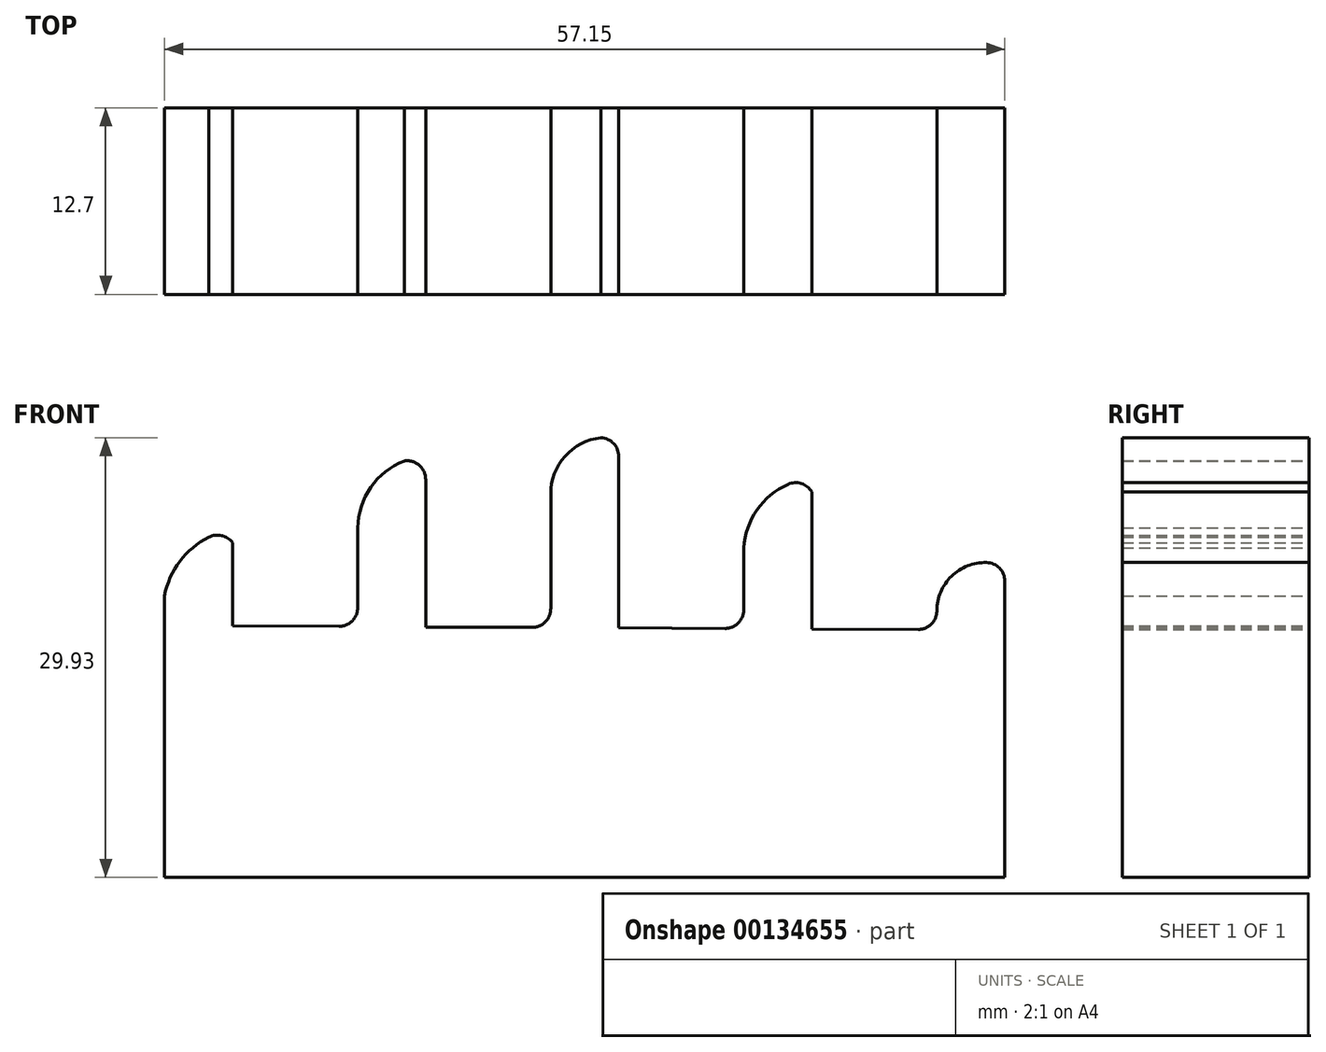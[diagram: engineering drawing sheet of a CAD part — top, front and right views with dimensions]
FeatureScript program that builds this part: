
annotation { "Feature Type Name" : "Feature", "Feature Type Description" : "" }
export const myFeature = defineFeature(function(context is Context, id is Id, definition is map)
    precondition{}
    {
        {
            var Q0;
            Q0=qCreatedBy(makeId("Front.planeOp"),FACE);
            var sketch = newSketch(context, id + "F0", { "sketchPlane" : qUnion([Q0])});
            skLineSegment(sketch, "E0", {"start": v(-7.96, 21.1) * mm, "end": v(-7.96, 21.1) * mm});
            skLineSegment(sketch, "E1", {"start": v(-8.39, 0) * mm, "end": v(-65.54, 0) * mm});
            skArc(sketch, "E2.filletArc", {"start": v(-23.14, 26.76) * mm, "mid": v(-25.25, 25) * mm, "end": v(-26.14, 22.42) * mm});
            skArc(sketch, "E3.filletArc", {"start": v(-60.92, 22.78) * mm, "mid": v(-61.66, 23.27) * mm, "end": v(-62.53, 23.15) * mm});
            skArc(sketch, "E4.filletArc", {"start": v(-47.78, 27.1) * mm, "mid": v(-48.23, 28.05) * mm, "end": v(-49.24, 28.35) * mm});
            skArc(sketch, "E5.filletArc", {"start": v(-34.65, 28.66) * mm, "mid": v(-35, 29.53) * mm, "end": v(-35.86, 29.93) * mm});
            skArc(sketch, "E6.filletArc", {"start": v(-21.52, 26.23) * mm, "mid": v(-22.23, 26.8) * mm, "end": v(-23.14, 26.76) * mm});
            skArc(sketch, "E7.filletArc", {"start": v(-8.39, 20.16) * mm, "mid": v(-8.75, 21.05) * mm, "end": v(-9.63, 21.43) * mm});
            skPoint(sketch, "E8.endSnap0", {"position": v(-36.53, 17) * mm});
            skLineSegment(sketch, "E9", {"start": v(-60.92, 22.78) * mm, "end": v(-60.92, 17.12) * mm});
            skLineSegment(sketch, "E10", {"start": v(-47.78, 27.1) * mm, "end": v(-47.78, 17.05) * mm});
            skLineSegment(sketch, "E11", {"start": v(-34.65, 28.66) * mm, "end": v(-34.65, 16.99) * mm});
            skLineSegment(sketch, "E12", {"start": v(-26.14, 22.42) * mm, "end": v(-26.14, 18.22) * mm});
            skLineSegment(sketch, "E13", {"start": v(-21.52, 26.23) * mm, "end": v(-21.52, 16.9) * mm});
            skLineSegment(sketch, "E14", {"start": v(-60.92, 17.12) * mm, "end": v(-53.68, 17.09) * mm});
            skLineSegment(sketch, "E15", {"start": v(-47.78, 17.05) * mm, "end": v(-40.55, 17.02) * mm});
            skLineSegment(sketch, "E16", {"start": v(-34.65, 16.99) * mm, "end": v(-27.42, 16.95) * mm});
            skLineSegment(sketch, "E17", {"start": v(-21.52, 16.9) * mm, "end": v(-14.29, 16.88) * mm});
            skArc(sketch, "E18.filletArc", {"start": v(-27.42, 16.95) * mm, "mid": v(-26.52, 17.32) * mm, "end": v(-26.14, 18.22) * mm});
            skArc(sketch, "E19.filletArc", {"start": v(-14.29, 16.88) * mm, "mid": v(-13.39, 17.25) * mm, "end": v(-13.01, 18.15) * mm});
            skArc(sketch, "E20.filletArc", {"start": v(-40.55, 17.02) * mm, "mid": v(-39.65, 17.39) * mm, "end": v(-39.27, 18.29) * mm});
            skArc(sketch, "E21.filletArc", {"start": v(-53.68, 17.09) * mm, "mid": v(-52.78, 17.46) * mm, "end": v(-52.4, 18.36) * mm});
            skArc(sketch, "E22", {"start": v(-35.86, 29.93) * mm, "mid": v(-38.3, 28.66) * mm, "end": v(-39.27, 26.09) * mm});
            skArc(sketch, "E23", {"start": v(-49.24, 28.35) * mm, "mid": v(-51.51, 26.55) * mm, "end": v(-52.4, 23.8) * mm});
            skLineSegment(sketch, "E24", {"start": v(-52.4, 23.8) * mm, "end": v(-52.4, 18.36) * mm});
            skLineSegment(sketch, "E25", {"start": v(-39.27, 26.09) * mm, "end": v(-39.27, 18.29) * mm});
            skArc(sketch, "E26", {"start": v(-62.53, 23.15) * mm, "mid": v(-64.5, 21.52) * mm, "end": v(-65.54, 19.17) * mm});
            skLineSegment(sketch, "E27", {"start": v(-65.54, 19.17) * mm, "end": v(-65.54, 0) * mm});
            skArc(sketch, "E28", {"start": v(-9.63, 21.43) * mm, "mid": v(-12.02, 20.5) * mm, "end": v(-13.01, 18.15) * mm});
            skLineSegment(sketch, "E29", {"start": v(-8.39, 20.16) * mm, "end": v(-8.39, 0) * mm});
            skSolve(sketch);
        }
        {
            var Q0;
            Q0 = qSketchRegion(id + "F0", true);
            extrude(context, id + "F1", {"entities" : qUnion([Q0]), "depth" : 12.7 * mm});
        }
    });
